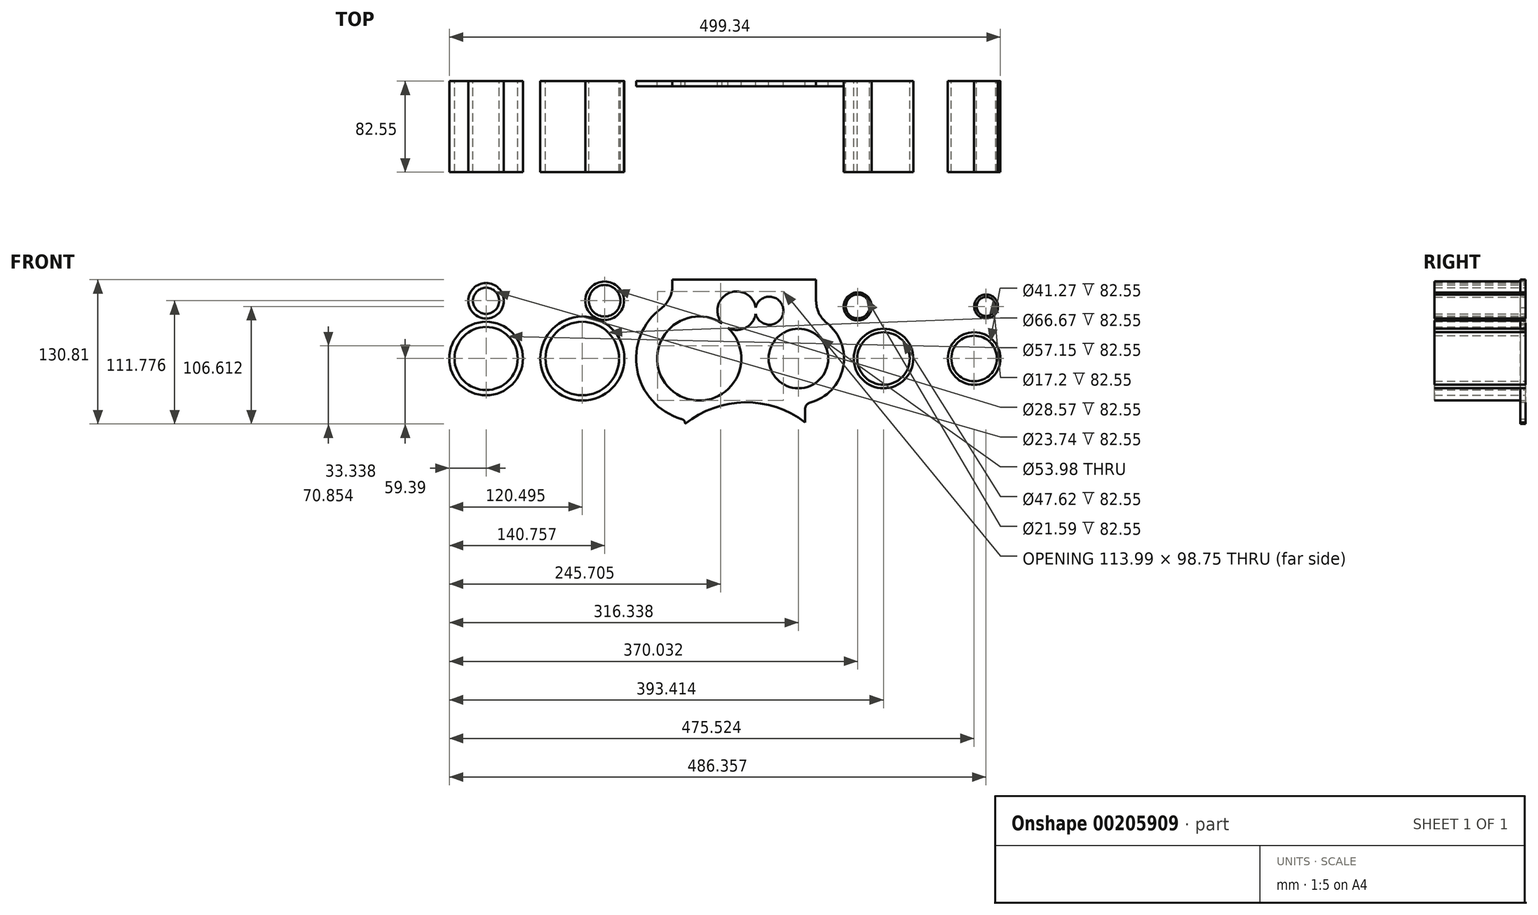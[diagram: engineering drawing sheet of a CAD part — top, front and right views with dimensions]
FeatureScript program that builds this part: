
annotation { "Feature Type Name" : "Feature", "Feature Type Description" : "" }
export const myFeature = defineFeature(function(context is Context, id is Id, definition is map)
    precondition{}
    {
        {
            var Q0;
            Q0=qCreatedBy(makeId("Front.planeOp"),FACE);
            var sketch = newSketch(context, id + "F0", { "sketchPlane" : qUnion([Q0])});
            skLineSegment(sketch, "E0", {"start": v(0, 126.18) * mm, "end": v(0, -127) * mm, "construction": true});
            skLineSegment(sketch, "E1", {"start": v(-98.09, 0) * mm, "end": v(109.13, 0) * mm, "construction": true});
            skArc(sketch, "E2", {"start": v(-76.8, 45.65) * mm, "mid": v(-98.66, -10.12) * mm, "end": v(-58.73, -54.77) * mm});
            skArc(sketch, "E3", {"start": v(58.21, -39.86) * mm, "mid": v(87.92, -8.35) * mm, "end": v(73.13, 32.35) * mm});
            skCircle(sketch, "E4", {"center": v(-42.42, 0) * mm, "radius": 38.1 * mm});
            skCircle(sketch, "E5", {"center": v(47.5, 0) * mm, "radius": 26.99 * mm});
            skLineSegment(sketch, "E6", {"start": v(63.5, 71.42) * mm, "end": v(-66.68, 71.42) * mm});
            skLineSegment(sketch, "E7", {"start": v(63.5, 71.42) * mm, "end": v(63.5, 52.26) * mm});
            skLineSegment(sketch, "E8", {"start": v(-66.68, 71.42) * mm, "end": v(-66.68, 65.94) * mm});
            skPoint(sketch, "E9.visualSharp", {"position": v(-66.68, 51.75) * mm});
            skArc(sketch, "E9.filletArc", {"start": v(-76.8, 45.65) * mm, "mid": v(-69.35, 54.6) * mm, "end": v(-66.68, 65.94) * mm});
            skPoint(sketch, "E10.visualSharp", {"position": v(63.5, 38.05) * mm});
            skArc(sketch, "E10.filletArc", {"start": v(63.5, 52.26) * mm, "mid": v(66.03, 41.2) * mm, "end": v(73.13, 32.35) * mm});
            skPoint(sketch, "E11.visualSharp", {"position": v(53.51, -40.83) * mm});
            skLineSegment(sketch, "E12", {"start": v(53.51, -46) * mm, "end": v(53.51, -54.97) * mm});
            skCircle(sketch, "E13", {"center": v(21.16, 43.38) * mm, "radius": 12.7 * mm});
            skCircle(sketch, "E14", {"center": v(-8.46, 43.38) * mm, "radius": 17.46 * mm});
            skLineSegment(sketch, "E15.bottom", {"start": v(-66.68, 71.42) * mm, "end": v(-66.68, 71.42) * mm});
            skLineSegment(sketch, "E16.bottom", {"start": v(63.03, 87.3) * mm, "end": v(63.5, 87.3) * mm});
            skLineSegment(sketch, "E16.top", {"start": v(63.03, 71.42) * mm, "end": v(63.5, 71.42) * mm});
            skArc(sketch, "E17.filletArc", {"start": v(58.21, -39.86) * mm, "mid": v(54.82, -42.13) * mm, "end": v(53.51, -46) * mm});
            skArc(sketch, "E18", {"start": v(53.51, -58) * mm, "mid": v(-1.1, -39.7) * mm, "end": v(-55.24, -59.39) * mm});
            skLineSegment(sketch, "E19", {"start": v(53.51, -54.97) * mm, "end": v(53.51, -58) * mm});
            skArc(sketch, "E20", {"start": v(-55.24, -59.39) * mm, "mid": v(-56.03, -56.36) * mm, "end": v(-58.73, -54.77) * mm});
            skSolve(sketch);
        }
        {
            var Q0;
            Q0=qSketchRegion(id+"F0",true);
            extrude(context, id + "F1", {"entities" : qUnion([Q0]), "depth" : 4.76 * mm});
        }
        {
            var Q0;
            Q0=qCreatedBy(makeId("Front.planeOp"),FACE);
            var sketch = newSketch(context, id + "F2", { "sketchPlane" : qUnion([Q0])});
            skCircle(sketch, "E21", {"center": v(-148.35, 0) * mm, "radius": 38.1 * mm});
            skCircle(sketch, "E22", {"center": v(-148.35, 0) * mm, "radius": 33.34 * mm});
            skCircle(sketch, "E23", {"center": v(-128.08, 52.39) * mm, "radius": 17.46 * mm});
            skCircle(sketch, "E24", {"center": v(-128.08, 52.39) * mm, "radius": 14.29 * mm});
            skCircle(sketch, "E25", {"center": v(124.57, 0) * mm, "radius": 26.99 * mm});
            skCircle(sketch, "E26", {"center": v(124.57, 0) * mm, "radius": 23.81 * mm});
            skCircle(sketch, "E27", {"center": v(101.2, 47.22) * mm, "radius": 12.7 * mm});
            skCircle(sketch, "E28", {"center": v(101.2, 47.22) * mm, "radius": 10.8 * mm});
            skCircle(sketch, "E29", {"center": v(-235.5, 0) * mm, "radius": 33.34 * mm});
            skCircle(sketch, "E30", {"center": v(-235.5, 0) * mm, "radius": 28.58 * mm});
            skCircle(sketch, "E31", {"center": v(-235.5, 52.39) * mm, "radius": 16.08 * mm});
            skCircle(sketch, "E32", {"center": v(-235.5, 52.39) * mm, "radius": 11.87 * mm});
            skCircle(sketch, "E33", {"center": v(206.68, 0) * mm, "radius": 23.81 * mm});
            skCircle(sketch, "E34", {"center": v(206.68, 0) * mm, "radius": 20.64 * mm});
            skCircle(sketch, "E35", {"center": v(217.52, 47.22) * mm, "radius": 10.8 * mm});
            skCircle(sketch, "E36", {"center": v(217.52, 47.22) * mm, "radius": 8.6 * mm});
            skSolve(sketch);
        }
        {
            var Q0;
            Q0=makeQuery(id+"F2.imprint","IMPRINT",FACE,{"disambiguationData":[TD([[makeQuery(id+"F2.imprint","IMPRINT",EDGE,{"derivedFrom":sQuery(id+"F2.wireOp",EDGE,"E31")}),1.0]])]});
            var Q1;
            Q1=makeQuery(id+"F2.imprint","IMPRINT",FACE,{"disambiguationData":[TD([[makeQuery(id+"F2.imprint","IMPRINT",EDGE,{"derivedFrom":sQuery(id+"F2.wireOp",EDGE,"E29")}),1.0]])]});
            var Q2;
            Q2=makeQuery(id+"F2.imprint","IMPRINT",FACE,{"disambiguationData":[TD([[makeQuery(id+"F2.imprint","IMPRINT",EDGE,{"derivedFrom":sQuery(id+"F2.wireOp",EDGE,"E21")}),1.0]])]});
            var Q3;
            Q3=makeQuery(id+"F2.imprint","IMPRINT",FACE,{"disambiguationData":[TD([[makeQuery(id+"F2.imprint","IMPRINT",EDGE,{"derivedFrom":sQuery(id+"F2.wireOp",EDGE,"E23")}),1.0]])]});
            var Q4;
            Q4=makeQuery(id+"F2.imprint","IMPRINT",FACE,{"disambiguationData":[TD([[makeQuery(id+"F2.imprint","IMPRINT",EDGE,{"derivedFrom":sQuery(id+"F2.wireOp",EDGE,"E27")}),1.0]])]});
            var Q5;
            Q5=makeQuery(id+"F2.imprint","IMPRINT",FACE,{"disambiguationData":[TD([[makeQuery(id+"F2.imprint","IMPRINT",EDGE,{"derivedFrom":sQuery(id+"F2.wireOp",EDGE,"E25")}),1.0]])]});
            var Q6;
            Q6=makeQuery(id+"F2.imprint","IMPRINT",FACE,{"disambiguationData":[TD([[makeQuery(id+"F2.imprint","IMPRINT",EDGE,{"derivedFrom":sQuery(id+"F2.wireOp",EDGE,"E33")}),1.0]])]});
            var Q7;
            Q7=makeQuery(id+"F2.imprint","IMPRINT",FACE,{"disambiguationData":[TD([[makeQuery(id+"F2.imprint","IMPRINT",EDGE,{"derivedFrom":sQuery(id+"F2.wireOp",EDGE,"E35")}),1.0]])]});
            extrude(context, id + "F3", {"entities" : qUnion([Q0, Q1, Q2, Q3, Q4, Q5, Q6, Q7]), "depth" : 82.55 * mm});
        }
    });
